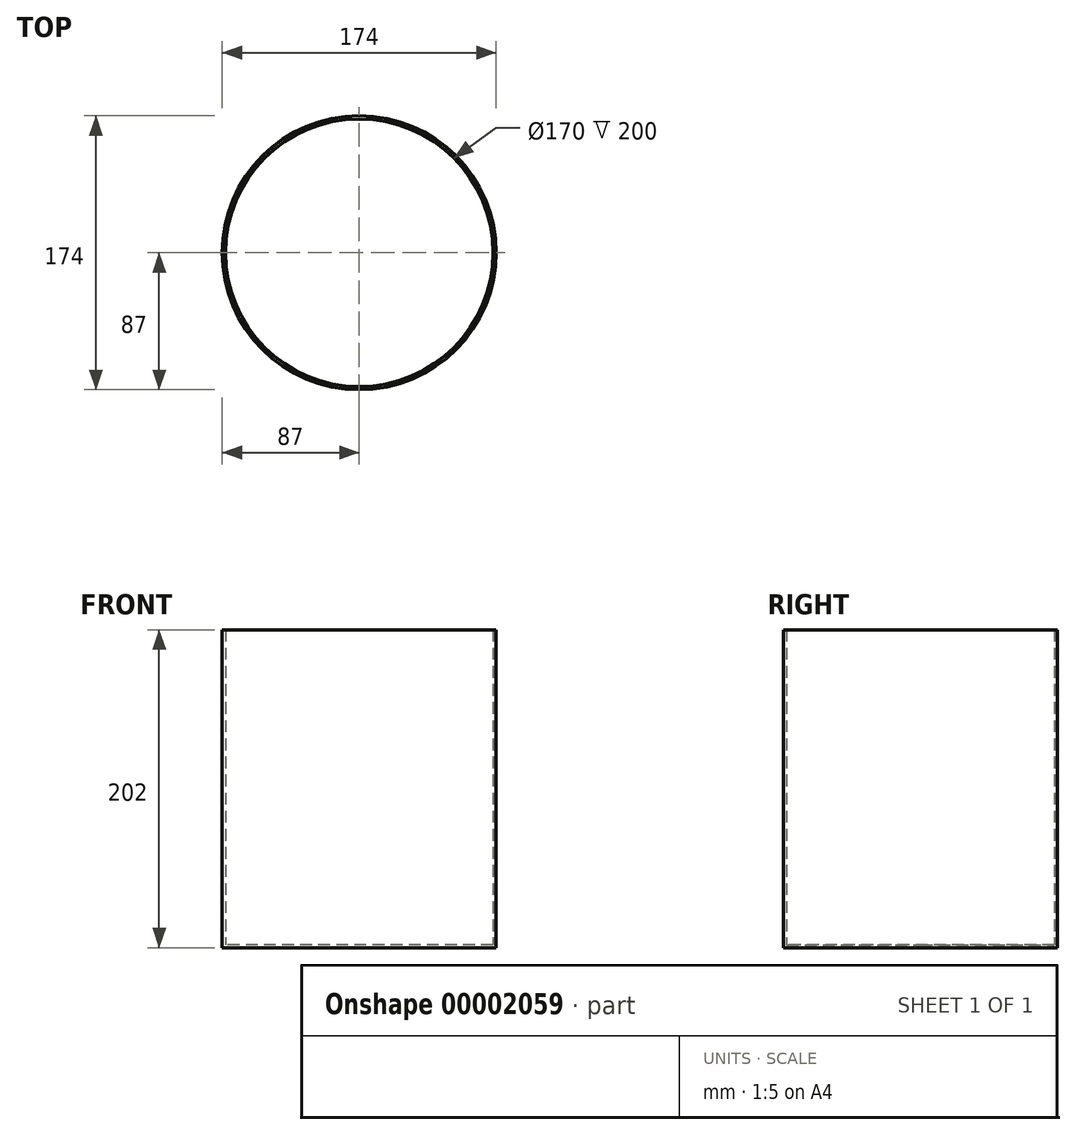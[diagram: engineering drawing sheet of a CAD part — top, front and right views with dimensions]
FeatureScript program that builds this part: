
annotation { "Feature Type Name" : "Feature", "Feature Type Description" : "" }
export const myFeature = defineFeature(function(context is Context, id is Id, definition is map)
    precondition{}
    {
        {
            var Q0;
            Q0=qCreatedBy(makeId("Top.planeOp"),FACE);
            var sketch = newSketch(context, id + "F0", { "sketchPlane" : qUnion([Q0])});
            skCircle(sketch, "E0", {"center": v(0, 0) * mm, "radius": 85 * mm});
            skCircle(sketch, "E1", {"center": v(0, 0) * mm, "radius": 87 * mm});
            skSolve(sketch);
        }
        {
            var Q0;
            Q0 = qSketchRegion(id + "F0", true);
            var Q1;
            Q1=makeQuery(id+"F0.imprint","IMPRINT",FACE,{"disambiguationData":[TD([[makeQuery(id+"F0.imprint","IMPRINT",EDGE,{"derivedFrom":sQuery(id+"F0.wireOp",EDGE,"E0")}),1.0]])]});
            extrude(context, id + "F1", {"entities" : qUnion([Q0, Q1]), "oppositeDirection" : true, "depth" : 2 * mm});
        }
        {
            var Q0;
            Q0=makeQuery(id+"F0.imprint","IMPRINT",FACE,{"disambiguationData":[TD([[makeQuery(id+"F0.imprint","IMPRINT",EDGE,{"derivedFrom":sQuery(id+"F0.wireOp",EDGE,"E0")}),-1.0]])]});
            extrude(context, id + "F2", {"entities" : qUnion([Q0]), "operationType" : NewBodyOperationType.ADD, "depth" : 200 * mm});
        }
    });
